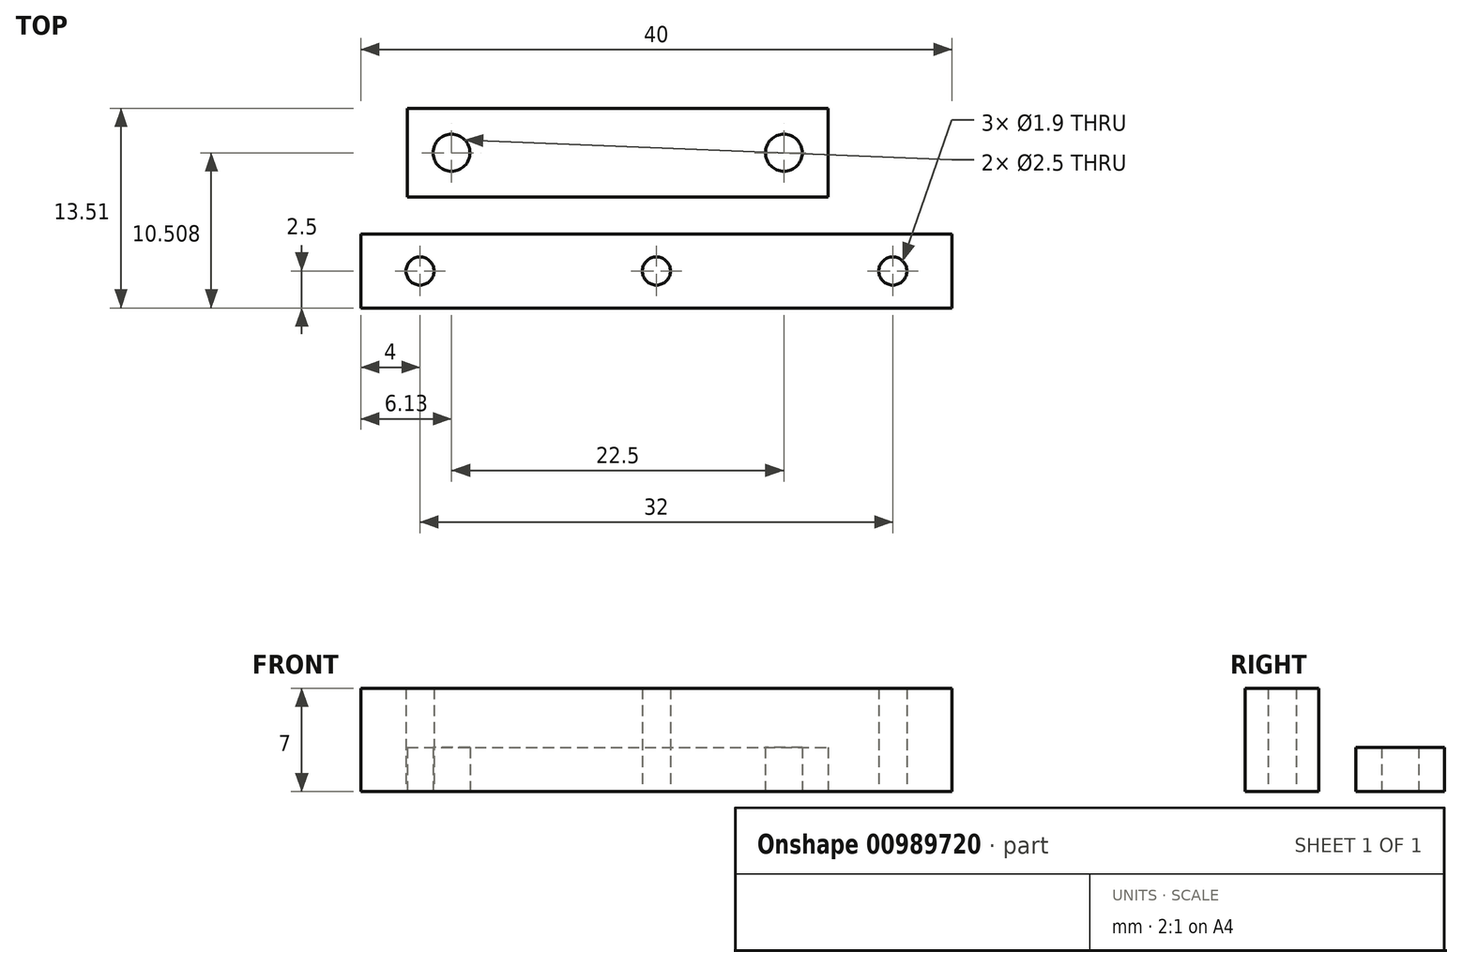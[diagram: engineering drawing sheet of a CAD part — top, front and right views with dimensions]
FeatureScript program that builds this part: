
annotation { "Feature Type Name" : "Feature", "Feature Type Description" : "" }
export const myFeature = defineFeature(function(context is Context, id is Id, definition is map)
    precondition{}
    {
        {
            var Q0;
            Q0=qCreatedBy(makeId("Top.planeOp"),FACE);
            var sketch = newSketch(context, id + "F0", { "sketchPlane" : qUnion([Q0])});
            skLineSegment(sketch, "E0.bottom", {"start": v(-20, 2.5) * mm, "end": v(20, 2.5) * mm});
            skLineSegment(sketch, "E0.top", {"start": v(-20, -2.5) * mm, "end": v(20, -2.5) * mm});
            skLineSegment(sketch, "E0.left", {"start": v(-20, 2.5) * mm, "end": v(-20, -2.5) * mm});
            skLineSegment(sketch, "E0.right", {"start": v(20, 2.5) * mm, "end": v(20, -2.5) * mm});
            skPoint(sketch, "E0.middle", {"position": v(0, 0) * mm});
            skCircle(sketch, "E1", {"center": v(-16, 0) * mm, "radius": 0.95 * mm});
            skCircle(sketch, "E2.1.0.0", {"center": v(0, 0) * mm, "radius": 0.95 * mm});
            skCircle(sketch, "E2.2.0.0", {"center": v(16, 0) * mm, "radius": 0.95 * mm});
            skLineSegment(sketch, "E2.direction1", {"start": v(-16, 0) * mm, "end": v(0, 0) * mm, "construction": true});
            skSolve(sketch);
        }
        {
            var Q0;
            Q0 = qSketchRegion(id + "F0", true);
            extrude(context, id + "F1", {"entities" : qUnion([Q0]), "depth" : 7 * mm, "offsetDistance" : 25 * mm});
        }
        {
            var Q0;
            Q0=qCreatedBy(makeId("Top.planeOp"),FACE);
            var sketch = newSketch(context, id + "F2", { "sketchPlane" : qUnion([Q0])});
            skCircle(sketch, "E3", {"center": v(-13.87, 8) * mm, "radius": 1.25 * mm});
            skCircle(sketch, "E4.1.0.0", {"center": v(8.63, 8) * mm, "radius": 1.25 * mm});
            skLineSegment(sketch, "E4.direction1", {"start": v(-13.87, 8) * mm, "end": v(8.63, 8) * mm, "construction": true});
            skLineSegment(sketch, "E5.bottom", {"start": v(-16.87, 11) * mm, "end": v(11.63, 11) * mm});
            skLineSegment(sketch, "E5.top", {"start": v(-16.87, 5) * mm, "end": v(11.63, 5) * mm});
            skLineSegment(sketch, "E5.left", {"start": v(-16.87, 11) * mm, "end": v(-16.87, 5) * mm});
            skLineSegment(sketch, "E5.right", {"start": v(11.63, 11) * mm, "end": v(11.63, 5) * mm});
            skSolve(sketch);
        }
        {
            var Q0;
            Q0 = qSketchRegion(id + "F2", true);
            extrude(context, id + "F3", {"entities" : qUnion([Q0]), "depth" : 3 * mm, "offsetDistance" : 25 * mm});
        }
    });
